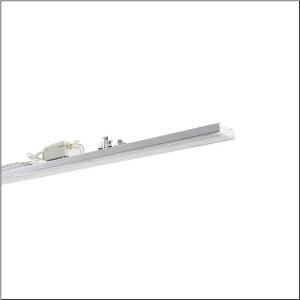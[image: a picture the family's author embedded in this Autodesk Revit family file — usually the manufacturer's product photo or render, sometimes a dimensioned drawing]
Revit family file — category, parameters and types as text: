
# Revit family: licross_11_recessed_mo_51te19dv4e5g
name_source: partatom
category: Lighting Fixtures
units: mm (PartAtom-declared; Revit-internal decimal feet)

## family parameters
Cut with Voids When Loaded = No
Host = Face
Light Source = No
Part Type = Normal
Room Calculation Point = No
Round Connector Dimension = Use Diameter
Shared = No

## types (1)
- --- (1 x LED, 14720 lm, 84.1 W, 4000K)
    Apparent Load = 84 VA
    CIE Flux Codes = 55 90 98 100 100
    Color Rendering = 80
    Color Temperature = 4000K
    Default Elevation = 1800 mm
    Description = Licross 11 Recessed MO, luminaire insert, of sheet steel, galvanised, coil coated, white, length: 2.250mm, width: 66mm, height: 67mm, LED rated luminous flux: 14.720lm, light colour: 840, SDCM (Standard Deviation of Colour Matching)MacAdam ≤ 2 SDCM (initial), control gear: DALI 2, with plug, 5-pole, with phase selection, mains connection: 220..240V, AC, 50/60Hz, rated input power: 84W, internal wiring halogen-free, primary light control with lens, of plastic, primary optical cover: cover, of PMMA, light emission: direct distribution, primary light characteristic: double asymmetric, protection rating (complete): IP54, insulation class (complete): insulation class I (protective earthing), certification: CE, ENEC, VDE, UKCA, protection symbol: D if used in an environment with non-conductive dust loads with corresponding accessories, impact resistance: IK06, permissible ambient temperature for indoor applications: -25..+35°C, corresponds to IFS (International Featured Standards) requirements for safety and quality in the food industry, reducing of maximum allowable ambient temperature of 5°C with ceiling mounting, LABS conformity tested according to VDMA 24364:2018-05, The light source and the operating device comply with the requirements of the Ecodesign Regulation (EU) 2019/2020 and are replaceable in accordance with this regulation, packaging unit: 1 piece
    Height = 58 mm
    Lamp = 1 x LED
    Lamp Light Flux = 14720 lm
    Lamp Power = 84.1 W
    Lamp count = 1
    Length = 2250 mm
    Luminous efficacy = 175 lm/W
    Manufacturer = Siteco
    ModVariant = No
    Model = 51TE19DV4E5G
    Mounting Place = Ceiling
    Mounting Type = Pendant
    Number of Poles = 1
    OnlyDefault = Yes
    Power Factor = 1
    Product Name = Licross 11 Recessed MO
    Product group = luminaire insert | ceiling pendant
    ProductGroupID = 901
    Protection Class = Protection class I
    Protection Degree = IP 54
    RLX_Detail_Level = 1
    RLX_Emergency_Light_Flux = 0 lm
    RLX_Emergency_Type = 0
    RLX_Emergency_Type_DB = No
    RlxData = <blob elided: 29789 chars, md5=6e4839b9>
    Socket = socket
    Standby Power = 0 W
    System Light Flux = 14720 lm
    System Power = 84 W
    Type Comments = factory setting: luminous flux: 100 % | dim-lin: 254 | 378 mA
    Type Image = l_1296930.jpg
    URL = http://relux.com
    VarID = @adj_103819
    Voltage = 0 V
    Weight = 0.00 kg
    Width = 66 mm

## geometry (parser evidence)
native form markers: Blend x4, Sweep x9
no freeform markers — native parametric forms only
